# Revit family: Sanitary_Toilet-Cisterns_hansgrohe_60271XXX-EluPura-Original-Q-Tank-side-in__00
name_source: partatom
category: Plumbing Fixtures
units: mm (PartAtom-declared; Revit-internal decimal feet)

## family parameters
Always vertical = No
Cut with Voids When Loaded = No
OmniClass Number = 23.31.19.19.19
OmniClass Title = Water Closet Tanks
Part Type = Normal
Room Calculation Point = No
Round Connector Dimension = Use Diameter
Shared = No
Work Plane-Based = Yes

## types (1)
- 450 White
    Connector Description = Water Inlet 12.7mm
    Default Elevation = 1219 mm
    Description = EluPura Original Q Tank side inlet
    Diameter = 13 mm
    Manufacturer = Hansgrohe
    Material 1 = Hansgrohe - Ceramic - 450 White
    Material 2 = Hansgrohe - Metal - 000 Chrome
    Model = 60271XXX
    Product Guid = d94a476b-4484-4e25-8609-842a9d370f1b
    Product Page URL = https://www.hansgrohe.com
    Product data url = https://bimobject.com
    URL = https://www.hansgrohe.com
    Version = 1

## geometry (parser evidence)
native form markers: Sweep x3
no freeform markers — native parametric forms only
